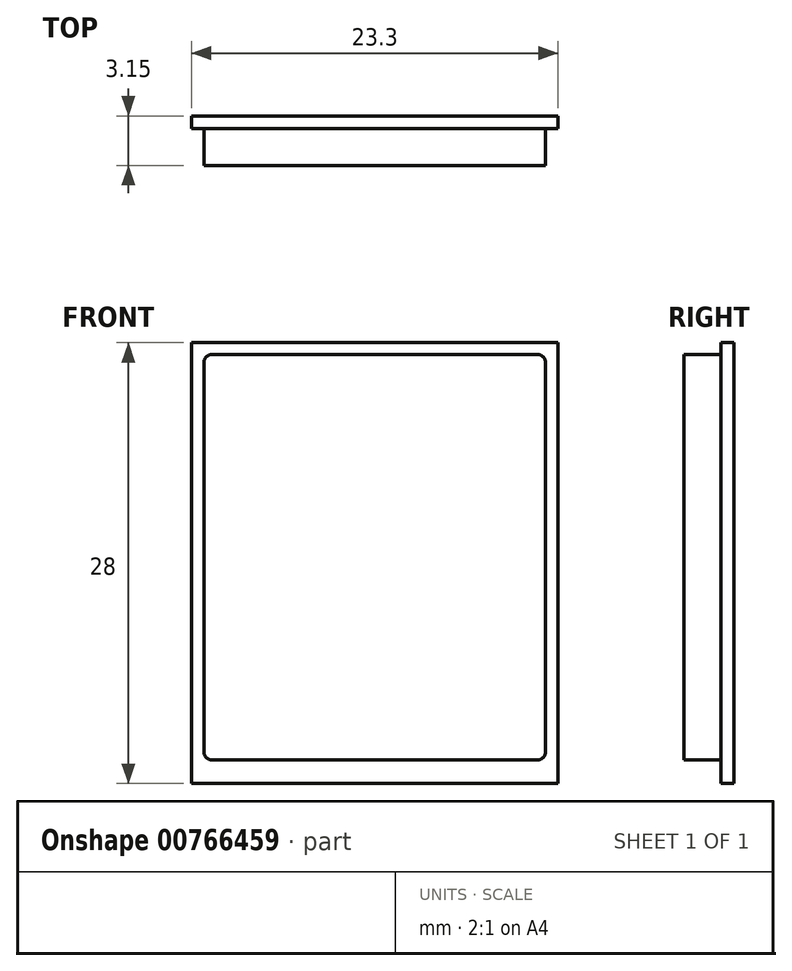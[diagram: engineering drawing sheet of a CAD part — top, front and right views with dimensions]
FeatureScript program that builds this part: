
annotation { "Feature Type Name" : "Feature", "Feature Type Description" : "" }
export const myFeature = defineFeature(function(context is Context, id is Id, definition is map)
    precondition{}
    {
        {
            var Q0;
            Q0=qCreatedBy(makeId("Front.planeOp"),FACE);
            var sketch = newSketch(context, id + "F0", { "sketchPlane" : qUnion([Q0])});
            skLineSegment(sketch, "E0.bottom", {"start": v(-11.65, 14) * mm, "end": v(11.65, 14) * mm});
            skLineSegment(sketch, "E0.top", {"start": v(-11.65, -14) * mm, "end": v(11.65, -14) * mm});
            skLineSegment(sketch, "E0.left", {"start": v(-11.65, 14) * mm, "end": v(-11.65, -14) * mm});
            skLineSegment(sketch, "E0.right", {"start": v(11.65, 14) * mm, "end": v(11.65, -14) * mm});
            skPoint(sketch, "E0.middle", {"position": v(0, 0) * mm});
            skSolve(sketch);
        }
        {
            var Q0;
            Q0 = qSketchRegion(id + "F0", true);
            extrude(context, id + "F1", {"entities" : qUnion([Q0]), "depth" : .8 * mm, "offsetDistance" : 25 * mm});
        }
        {
            var Q0;
            Q0=makeQuery(id+"F1.opExtrude","CAP_FACE",FACE,{"disambiguationData":[OSD([sQuery(id+"F0.wireOp",EDGE,"E0.bottom"),sQuery(id+"F0.wireOp",EDGE,"E0.top"),sQuery(id+"F0.wireOp",EDGE,"E0.left"),sQuery(id+"F0.wireOp",EDGE,"E0.right")])],"isStart":false});
            var sketch = newSketch(context, id + "F2", { "sketchPlane" : qUnion([Q0])});
            skLineSegment(sketch, "E1.bottom", {"start": v(-10.85, 13.25) * mm, "end": v(10.85, 13.25) * mm});
            skLineSegment(sketch, "E1.top", {"start": v(-10.85, -12.5) * mm, "end": v(10.85, -12.5) * mm});
            skLineSegment(sketch, "E1.left", {"start": v(-10.85, 13.25) * mm, "end": v(-10.85, -12.5) * mm});
            skLineSegment(sketch, "E1.right", {"start": v(10.85, 13.25) * mm, "end": v(10.85, -12.5) * mm});
            skSolve(sketch);
        }
        {
            var Q0;
            Q0 = qSketchRegion(id + "F2", true);
            extrude(context, id + "F3", {"entities" : qUnion([Q0]), "operationType" : NewBodyOperationType.ADD, "depth" : 2.35 * mm, "offsetDistance" : 25 * mm});
        }
        {
            var Q0;
            Q0=makeQuery(id+"F3.opExtrude","SWEPT_EDGE",EDGE,{"disambiguationData":[OSD([sQuery(id+"F2.wireOp",EDGE,"E1.top"),sQuery(id+"F2.wireOp",EDGE,"E1.left")])]});
            var Q1;
            Q1=makeQuery(id+"F3.opExtrude","SWEPT_EDGE",EDGE,{"disambiguationData":[OSD([sQuery(id+"F2.wireOp",EDGE,"E1.top"),sQuery(id+"F2.wireOp",EDGE,"E1.right")])]});
            var Q2;
            Q2=makeQuery(id+"F3.opExtrude","SWEPT_EDGE",EDGE,{"disambiguationData":[OSD([sQuery(id+"F2.wireOp",EDGE,"E1.bottom"),sQuery(id+"F2.wireOp",EDGE,"E1.right")])]});
            var Q3;
            Q3=makeQuery(id+"F3.opExtrude","SWEPT_EDGE",EDGE,{"disambiguationData":[OSD([sQuery(id+"F2.wireOp",EDGE,"E1.bottom"),sQuery(id+"F2.wireOp",EDGE,"E1.left")])]});
            fillet(context, id + "F4", {"entities" : qUnion([Q0, Q1, Q2, Q3]), "radius" : 0.5 * mm, "tangentPropagation" : true, "allowEdgeOverflow" : false});
        }
    });
